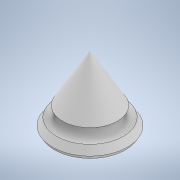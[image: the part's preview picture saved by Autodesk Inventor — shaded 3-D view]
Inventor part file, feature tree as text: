
AUTODESK INVENTOR PART (.ipt)
format: ipt  version: 2020 (Build 240168000, 168)  size: 151,040 bytes
history: native  units: mm
features: sketch x3, extrude x2, revolve x1, chamfer x1, projected_geometry x1
ambient origin geometry x8: Origin, YZ Plane, XZ Plane, XY Plane, X Axis, Y Axis, Z Axis, Center Point
bodies: Solid1 (feature_tree)
feature tree (8):
  extrude  "Extrusion1"  Depth=4.3mm
  extrude  "Extrusion2"  Depth=4.3mm
  revolve  "Revolution1"  [1 undecoded]
  chamfer  "Chamfer1"  Distance=4.0mm
  sketch  "Sketch1"  dims[d0=20.0mm d1=4.3mm]
  sketch  "Sketch2"  dims[d2=20.0mm d3=-5.235988mm d4=4.3mm]
  sketch  "Sketch3"  dims[d5=8.0mm d6=0.0mm d7=3.0mm d8=4.0mm d9=90.0deg d10=1.0mm d11=2.0mm d12=45.0deg]
  projected_geometry  "Projected Loop1"
note: 1 required parameter value undecoded (feature->parameter linkage not recoverable at this tier; creation-order binding heuristic only, values carry confidence <= 0.55)
